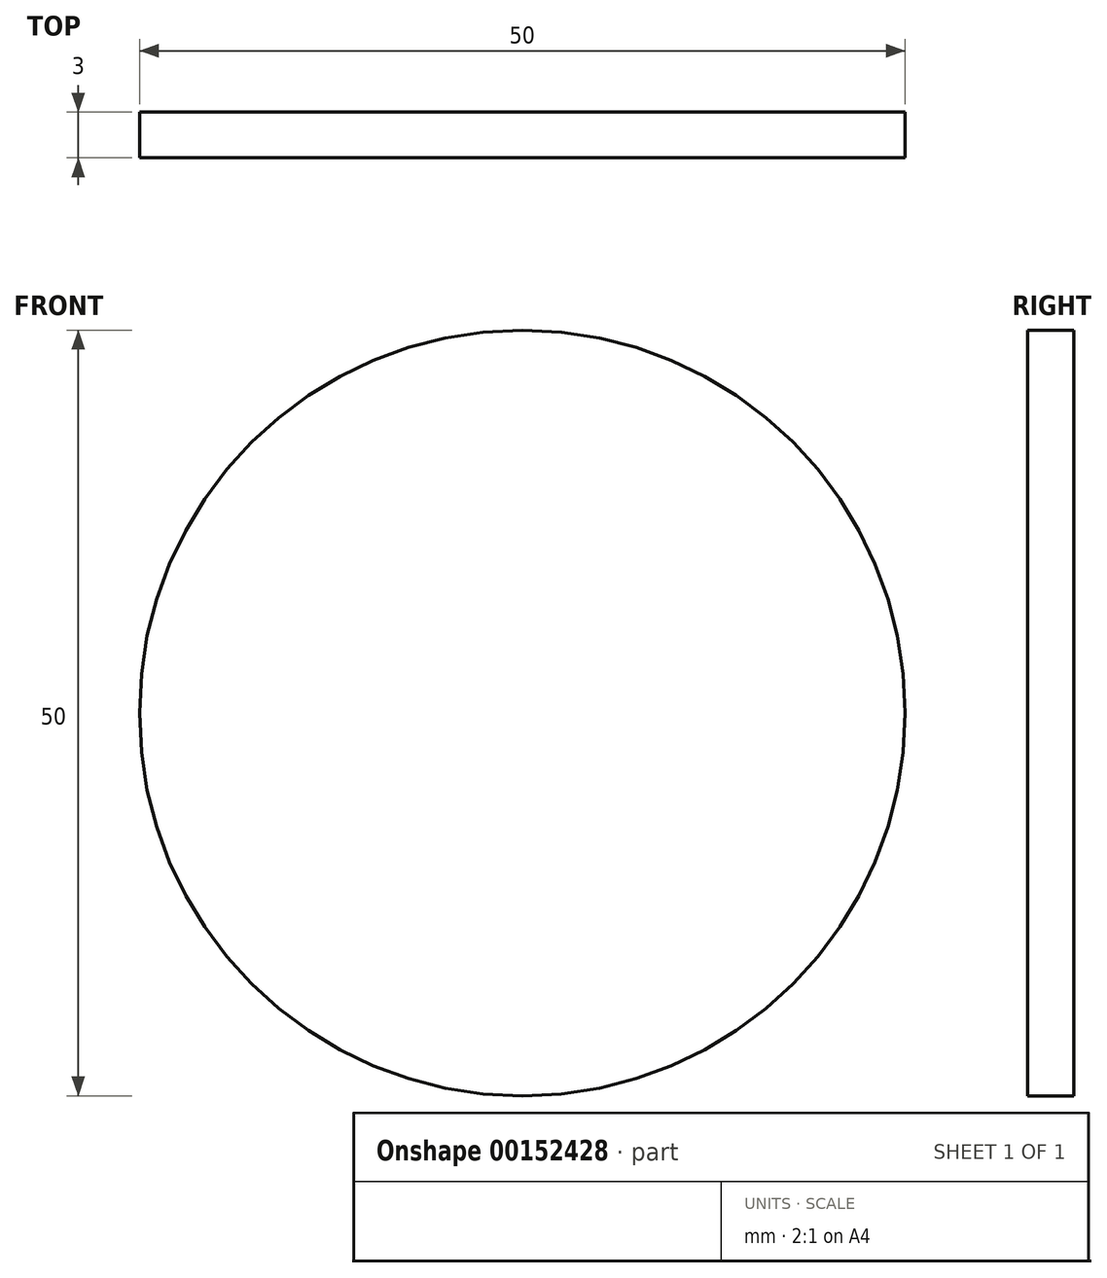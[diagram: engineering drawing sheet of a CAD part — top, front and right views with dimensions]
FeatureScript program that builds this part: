
annotation { "Feature Type Name" : "Feature", "Feature Type Description" : "" }
export const myFeature = defineFeature(function(context is Context, id is Id, definition is map)
    precondition{}
    {
        {
            var Q0;
            Q0=qCreatedBy(makeId("Front.planeOp"),FACE);
            var sketch = newSketch(context, id + "F0", { "sketchPlane" : qUnion([Q0])});
            skCircle(sketch, "E0", {"center": v(0, 0) * mm, "radius": 25 * mm});
            skSolve(sketch);
        }
        {
            var Q0;
            Q0=makeQuery(id+"F0.imprint","IMPRINT",FACE,{"disambiguationData":[TD([[makeQuery(id+"F0.imprint","IMPRINT",EDGE,{"derivedFrom":sQuery(id+"F0.wireOp",EDGE,"E0")}),1.0]])]});
            extrude(context, id + "F1", {"entities" : qUnion([Q0]), "depth" : 3 * mm});
        }
    });
